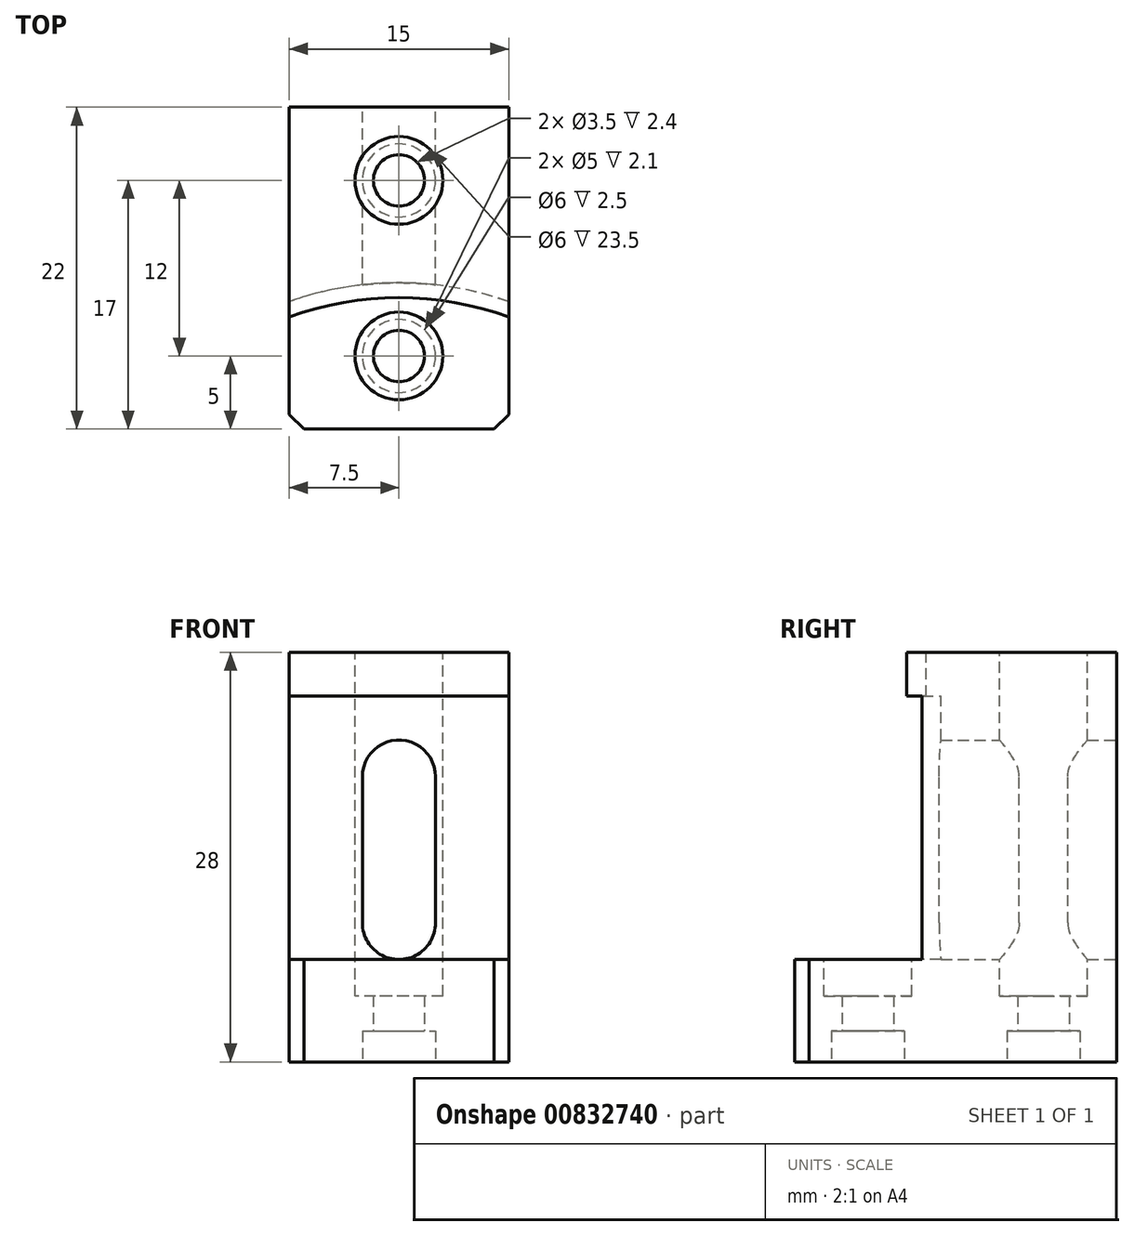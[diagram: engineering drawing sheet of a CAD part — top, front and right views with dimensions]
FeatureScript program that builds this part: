
annotation { "Feature Type Name" : "Feature", "Feature Type Description" : "" }
export const myFeature = defineFeature(function(context is Context, id is Id, definition is map)
    precondition{}
    {
        {
            var Q0;
            Q0=qCreatedBy(makeId("Top.planeOp"),FACE);
            var sketch = newSketch(context, id + "F0", { "sketchPlane" : qUnion([Q0])});
            skLineSegment(sketch, "E0.bottom", {"start": v(-7.5, -11) * mm, "end": v(7.5, -11) * mm});
            skLineSegment(sketch, "E0.top", {"start": v(-7.5, 11) * mm, "end": v(7.5, 11) * mm});
            skLineSegment(sketch, "E0.left", {"start": v(-7.5, -11) * mm, "end": v(-7.5, 11) * mm});
            skLineSegment(sketch, "E0.right", {"start": v(7.5, -11) * mm, "end": v(7.5, 11) * mm});
            skPoint(sketch, "E0.middle", {"position": v(0, 0) * mm});
            skSolve(sketch);
        }
        {
            var Q0;
            Q0=makeQuery(id+"F0.imprint","IMPRINT",FACE,{"disambiguationData":[TD([[makeQuery(id+"F0.imprint","IMPRINT",EDGE,{"derivedFrom":sQuery(id+"F0.wireOp",EDGE,"E0.bottom")}),1.0]])]});
            extrude(context, id + "F1", {"entities" : qUnion([Q0]), "depth" : 28 * mm, "offsetDistance" : 25 * mm});
        }
        {
            var Q0;
            Q0=makeQuery(id+"F1.opExtrude","CAP_FACE",FACE,{"disambiguationData":[OSD([sQuery(id+"F0.wireOp",EDGE,"E0.bottom"),sQuery(id+"F0.wireOp",EDGE,"E0.top"),sQuery(id+"F0.wireOp",EDGE,"E0.left"),sQuery(id+"F0.wireOp",EDGE,"E0.right")])],"isStart":false});
            var sketch = newSketch(context, id + "F2", { "sketchPlane" : qUnion([Q0])});
            skLineSegment(sketch, "E1.0", {"start": v(-7.5, -2) * mm, "end": v(7.5, -2) * mm});
            skCircle(sketch, "E2", {"center": v(0, -23.5) * mm, "radius": 21.5 * mm});
            skPoint(sketch, "E3", {"position": v(0, -2) * mm});
            skSolve(sketch);
        }
        {
            var Q0;
            {var subQ5=makeQuery(id+"F1.opExtrude","CAP_EDGE",EDGE,{"disambiguationData":[OSD([sQuery(id+"F0.wireOp",EDGE,"E0.bottom")])],"isStart":false});Q0=makeQuery(id+"F2.imprint","IMPRINT",FACE,{"disambiguationData":[TD([[makeQuery(id+"F2.imprint","IMPRINT",EDGE,{"derivedFrom":subQ5}),-1.0]])]});}
            var Q1;
            {var subQ1=makeQuery(id+"F1.opExtrude","CAP_EDGE",EDGE,{"disambiguationData":[OSD([sQuery(id+"F0.wireOp",EDGE,"E0.bottom")])],"isStart":false});Q1=makeQuery(id+"F2.imprint","IMPRINT",FACE,{"disambiguationData":[TD([[makeQuery(id+"F2.imprint","IMPRINT",EDGE,{"derivedFrom":subQ1}),1.0]])]});}
            extrude(context, id + "F3", {"entities" : qUnion([Q0, Q1]), "operationType" : NewBodyOperationType.REMOVE, "oppositeDirection" : true, "depth" : 3 * mm, "offsetDistance" : 25 * mm});
        }
        {
            var Q0;
            Q0=makeQuery(id+"F3.boolean.opBoolean","COPY",FACE,{"derivedFrom":makeQuery(id+"F3.opExtrude","CAP_FACE",FACE,{"disambiguationData":[OSD([sQuery(id+"F2.wireOp",EDGE,"E2")])],"isStart":false})});
            var sketch = newSketch(context, id + "F4", { "sketchPlane" : qUnion([Q0])});
            skCircle(sketch, "E4", {"center": v(0, -23.5) * mm, "radius": 22.5 * mm});
            skSolve(sketch);
        }
        {
            var Q0;
            Q0 = qSketchRegion(id + "F4", true);
            extrude(context, id + "F5", {"entities" : qUnion([Q0]), "operationType" : NewBodyOperationType.REMOVE, "oppositeDirection" : true, "depth" : 18 * mm, "offsetDistance" : 25 * mm});
        }
        {
            var Q0;
            Q0=makeQuery(id+"F1.opExtrude","SWEPT_FACE",FACE,{"disambiguationData":[OSD([sQuery(id+"F0.wireOp",EDGE,"E0.top")])]});
            var sketch = newSketch(context, id + "F6", { "sketchPlane" : qUnion([Q0])});
            skLineSegment(sketch, "E5.0", {"start": v(7.5, 7) * mm, "end": v(-7.5, 7) * mm, "construction": true});
            skArc(sketch, "E6", {"start": v(-2.5, 9.5) * mm, "mid": v(0, 7) * mm, "end": v(2.5, 9.5) * mm});
            skLineSegment(sketch, "E7.0", {"start": v(7.5, 22) * mm, "end": v(-7.5, 22) * mm, "construction": true});
            skArc(sketch, "E8", {"start": v(2.5, 19.5) * mm, "mid": v(0, 22) * mm, "end": v(-2.5, 19.5) * mm});
            skPoint(sketch, "E9", {"position": v(-2.5, 19.5) * mm});
            skPoint(sketch, "E10", {"position": v(2.5, 19.5) * mm});
            skPoint(sketch, "E11", {"position": v(-2.5, 9.5) * mm});
            skPoint(sketch, "E12", {"position": v(2.5, 9.5) * mm});
            skLineSegment(sketch, "E13", {"start": v(-2.5, 19.5) * mm, "end": v(-2.5, 9.5) * mm});
            skLineSegment(sketch, "E14", {"start": v(2.5, 19.5) * mm, "end": v(2.5, 9.5) * mm});
            skSolve(sketch);
        }
        {
            var Q0;
            Q0=makeQuery(id+"F6.imprint","IMPRINT",FACE,{"disambiguationData":[TD([[makeQuery(id+"F6.imprint","IMPRINT",EDGE,{"derivedFrom":sQuery(id+"F6.wireOp",EDGE,"E6")}),1.0]])]});
            extrude(context, id + "F7", {"entities" : qUnion([Q0]), "operationType" : NewBodyOperationType.REMOVE, "endBound" : BoundingType.UP_TO_NEXT, "oppositeDirection" : true, "depth" : 25 * mm, "offsetDistance" : 25 * mm});
        }
        {
            var Q0;
            Q0=makeQuery(id+"F1.opExtrude","CAP_FACE",FACE,{"disambiguationData":[OSD([sQuery(id+"F0.wireOp",EDGE,"E0.bottom"),sQuery(id+"F0.wireOp",EDGE,"E0.top"),sQuery(id+"F0.wireOp",EDGE,"E0.left"),sQuery(id+"F0.wireOp",EDGE,"E0.right")])],"isStart":true});
            var sketch = newSketch(context, id + "F8", { "sketchPlane" : qUnion([Q0])});
            skLineSegment(sketch, "E15.0", {"start": v(-7.5, -6) * mm, "end": v(7.5, -6) * mm, "construction": true});
            skLineSegment(sketch, "E16.0", {"start": v(-7.5, 6) * mm, "end": v(7.5, 6) * mm, "construction": true});
            skCircle(sketch, "E17", {"center": v(0, 6) * mm, "radius": 1.75 * mm});
            skCircle(sketch, "E18", {"center": v(0, 6) * mm, "radius": 2.5 * mm});
            skCircle(sketch, "E19", {"center": v(0, -6) * mm, "radius": 1.75 * mm});
            skCircle(sketch, "E20", {"center": v(0, -6) * mm, "radius": 2.5 * mm});
            skSolve(sketch);
        }
        {
            var Q0;
            Q0=makeQuery(id+"F8.imprint","IMPRINT",FACE,{"disambiguationData":[TD([[makeQuery(id+"F8.imprint","IMPRINT",EDGE,{"derivedFrom":sQuery(id+"F8.wireOp",EDGE,"E17")}),-1.0]])]});
            var Q1;
            Q1=makeQuery(id+"F8.imprint","IMPRINT",FACE,{"disambiguationData":[TD([[makeQuery(id+"F8.imprint","IMPRINT",EDGE,{"derivedFrom":sQuery(id+"F8.wireOp",EDGE,"E19")}),-1.0]])]});
            extrude(context, id + "F9", {"entities" : qUnion([Q0, Q1]), "operationType" : NewBodyOperationType.REMOVE, "oppositeDirection" : true, "depth" : 2.1 * mm, "offsetDistance" : 25 * mm});
        }
        {
            var Q0;
            Q0=makeQuery(id+"F9.boolean.opBoolean","SPLIT",FACE,{"disambiguationData":[TD([makeQuery(id+"F9.opExtrude","SWEPT_FACE",FACE,{"disambiguationData":[OSD([sQuery(id+"F8.wireOp",EDGE,"E19")])]})])],"derivedFrom":makeQuery(id+"F1.opExtrude","CAP_FACE",FACE,{"disambiguationData":[OSD([sQuery(id+"F0.wireOp",EDGE,"E0.bottom"),sQuery(id+"F0.wireOp",EDGE,"E0.top"),sQuery(id+"F0.wireOp",EDGE,"E0.left"),sQuery(id+"F0.wireOp",EDGE,"E0.right")])],"isStart":true})});
            var Q1;
            Q1=makeQuery(id+"F9.boolean.opBoolean","SPLIT",FACE,{"disambiguationData":[TD([makeQuery(id+"F9.opExtrude","SWEPT_FACE",FACE,{"disambiguationData":[OSD([sQuery(id+"F8.wireOp",EDGE,"E17")])]})])],"derivedFrom":makeQuery(id+"F1.opExtrude","CAP_FACE",FACE,{"disambiguationData":[OSD([sQuery(id+"F0.wireOp",EDGE,"E0.bottom"),sQuery(id+"F0.wireOp",EDGE,"E0.top"),sQuery(id+"F0.wireOp",EDGE,"E0.left"),sQuery(id+"F0.wireOp",EDGE,"E0.right")])],"isStart":true})});
            extrude(context, id + "F10", {"entities" : qUnion([Q0, Q1]), "operationType" : NewBodyOperationType.REMOVE, "endBound" : BoundingType.UP_TO_NEXT, "oppositeDirection" : true, "depth" : 25 * mm, "offsetDistance" : 25 * mm});
        }
        {
            var Q0;
            Q0=makeQuery(id+"F5.boolean.opBoolean","COPY",FACE,{"derivedFrom":makeQuery(id+"F5.opExtrude","CAP_FACE",FACE,{"disambiguationData":[OSD([sQuery(id+"F4.wireOp",EDGE,"E4")])],"isStart":false})});
            var sketch = newSketch(context, id + "F11", { "sketchPlane" : qUnion([Q0])});
            skCircle(sketch, "E21", {"center": v(0, -6) * mm, "radius": 3 * mm});
            skSolve(sketch);
        }
        {
            var Q0;
            Q0=makeQuery(id+"F11.imprint","IMPRINT",FACE,{"disambiguationData":[TD([[makeQuery(id+"F11.imprint","IMPRINT",EDGE,{"derivedFrom":sQuery(id+"F11.wireOp",EDGE,"E21")}),1.0]])]});
            var Q1;
            Q1=sQuery(id+"F11.wireOp",EDGE,"E21");
            extrude(context, id + "F12", {"entities" : qUnion([Q0]), "operationType" : NewBodyOperationType.REMOVE, "surfaceEntities" : qUnion([Q1]), "oppositeDirection" : true, "depth" : 2.5 * mm, "offsetDistance" : 25 * mm});
        }
        {
            var Q0;
            Q0=makeQuery(id+"F1.opExtrude","CAP_FACE",FACE,{"disambiguationData":[OSD([sQuery(id+"F0.wireOp",EDGE,"E0.bottom"),sQuery(id+"F0.wireOp",EDGE,"E0.top"),sQuery(id+"F0.wireOp",EDGE,"E0.left"),sQuery(id+"F0.wireOp",EDGE,"E0.right")])],"isStart":false});
            var sketch = newSketch(context, id + "F13", { "sketchPlane" : qUnion([Q0])});
            skLineSegment(sketch, "E22.0", {"start": v(-7.5, 6) * mm, "end": v(7.5, 6) * mm, "construction": true});
            skCircle(sketch, "E23", {"center": v(0, 6) * mm, "radius": 3 * mm});
            skSolve(sketch);
        }
        {
            var Q0;
            Q0=makeQuery(id+"F13.imprint","IMPRINT",FACE,{"disambiguationData":[TD([[makeQuery(id+"F13.imprint","IMPRINT",EDGE,{"derivedFrom":sQuery(id+"F13.wireOp",EDGE,"E23")}),1.0]])]});
            extrude(context, id + "F14", {"entities" : qUnion([Q0]), "operationType" : NewBodyOperationType.REMOVE, "oppositeDirection" : true, "depth" : 23.5 * mm, "offsetDistance" : 25 * mm});
        }
        {
            var Q0;
            Q0=makeQuery(id+"F1.opExtrude","SWEPT_EDGE",EDGE,{"disambiguationData":[OSD([sQuery(id+"F0.wireOp",EDGE,"E0.bottom"),sQuery(id+"F0.wireOp",EDGE,"E0.right")])]});
            var Q1;
            Q1=makeQuery(id+"F1.opExtrude","SWEPT_EDGE",EDGE,{"disambiguationData":[OSD([sQuery(id+"F0.wireOp",EDGE,"E0.bottom"),sQuery(id+"F0.wireOp",EDGE,"E0.left")])]});
            chamfer(context, id + "F15", {"entities" : qUnion([Q0, Q1]), "width" : 1 * mm, "tangentPropagation" : true});
        }
    });
